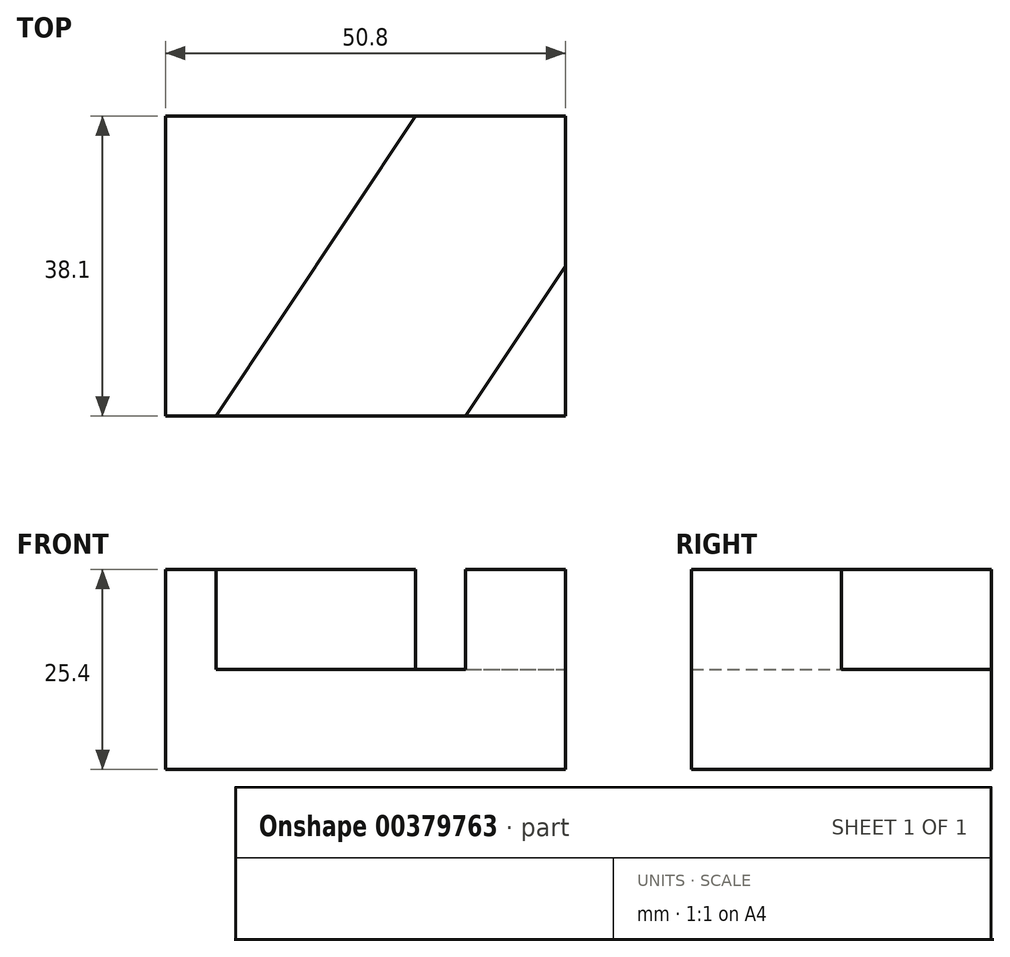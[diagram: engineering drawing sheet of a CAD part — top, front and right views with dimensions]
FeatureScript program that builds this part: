
annotation { "Feature Type Name" : "Feature", "Feature Type Description" : "" }
export const myFeature = defineFeature(function(context is Context, id is Id, definition is map)
    precondition{}
    {
        {
            var Q0;
            Q0=qCreatedBy(makeId("Top.planeOp"),FACE);
            var sketch = newSketch(context, id + "F0", { "sketchPlane" : qUnion([Q0])});
            skLineSegment(sketch, "E0", {"start": v(-49.64, 0) * mm, "end": v(-49.64, 38.1) * mm});
            skLineSegment(sketch, "E1", {"start": v(-49.64, 38.1) * mm, "end": v(1.16, 38.1) * mm});
            skLineSegment(sketch, "E2", {"start": v(1.16, 38.1) * mm, "end": v(1.16, 0) * mm});
            skLineSegment(sketch, "E3", {"start": v(-49.64, 0) * mm, "end": v(1.16, 0) * mm});
            skSolve(sketch);
        }
        {
            var Q0;
            Q0=makeQuery(id+"F0.imprint","IMPRINT",FACE,{"disambiguationData":[TD([[makeQuery(id+"F0.imprint","IMPRINT",EDGE,{"derivedFrom":sQuery(id+"F0.wireOp",EDGE,"E0")}),-1.0]])]});
            extrude(context, id + "F1", {"entities" : qUnion([Q0]), "depth" : 25.4 * mm});
        }
        {
            var Q0;
            Q0=makeQuery(id+"F1.opExtrude","CAP_FACE",FACE,{"disambiguationData":[OSD([sQuery(id+"F0.wireOp",EDGE,"E0"),sQuery(id+"F0.wireOp",EDGE,"E1"),sQuery(id+"F0.wireOp",EDGE,"E2"),sQuery(id+"F0.wireOp",EDGE,"E3")])],"isStart":false});
            var sketch = newSketch(context, id + "F2", { "sketchPlane" : qUnion([Q0])});
            skLineSegment(sketch, "E4", {"start": v(-49.64, 0) * mm, "end": v(-43.22, 0) * mm});
            skLineSegment(sketch, "E5", {"start": v(1.16, 38.1) * mm, "end": v(-17.9, 38.1) * mm});
            skLineSegment(sketch, "E6", {"start": v(-43.22, 0) * mm, "end": v(-17.9, 38.1) * mm});
            skLineSegment(sketch, "E7", {"start": v(1.16, 0) * mm, "end": v(-11.54, 0) * mm});
            skLineSegment(sketch, "E8", {"start": v(1.16, 0) * mm, "end": v(1.16, 19.05) * mm});
            skLineSegment(sketch, "E9", {"start": v(-11.54, 0) * mm, "end": v(1.16, 19.05) * mm});
            skSolve(sketch);
        }
        {
            var Q0;
            {var subQ0=sQuery(id+"F2.wireOp",EDGE,"E5");Q0=makeQuery(id+"F2.imprint","IMPRINT",FACE,{"disambiguationData":[TD([[makeQuery(id+"F2.imprint","IMPRINT",EDGE,{"derivedFrom":subQ0}),-1.0]])]});}
            extrude(context, id + "F3", {"entities" : qUnion([Q0]), "operationType" : NewBodyOperationType.REMOVE, "oppositeDirection" : true, "depth" : 12.7 * mm});
        }
    });
